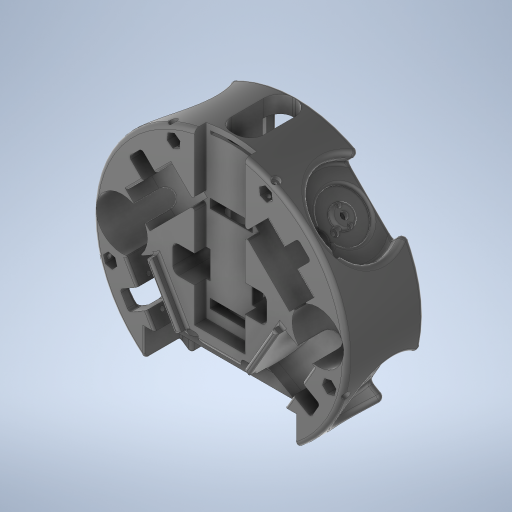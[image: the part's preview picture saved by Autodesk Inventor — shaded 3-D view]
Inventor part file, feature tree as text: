
AUTODESK INVENTOR PART (.ipt)
format: ipt  version: 2023 (Build 270158000, 158)  size: 3,632,128 bytes
history: native  units: mm
features: extrude x76, sketch x74, projected_geometry x35, fillet x19, other x9, chamfer x4, plane x2, mirror x1
ambient origin geometry x8: Origin, YZ Plane, XZ Plane, XY Plane, X Axis, Y Axis, Z Axis, Center Point
bodies: Solid1 (feature_tree)
feature tree (220):
  extrude  "Cilinder"  Depth=54.0mm TaperAngle=0.0deg
  other  "Motor Axis"
  other  "Plano M1"
  other  "Plano M2"
  other  "Plano M3"
  other  "Plano M4"
  extrude  "Roda M1"  Depth=176.0mm
  extrude  "Roda M2"  TaperAngle=60.0deg  [1 undecoded]
  extrude  "Roda M3"  TaperAngle=45.0deg  [1 undecoded]
  extrude  "Roda M4"  TaperAngle=0.0deg  [1 undecoded]
  extrude  "MotorsFitting"  Depth=14.6mm TaperAngle=0.0deg
  fillet  "MotorsCurve"  Radius=55.0mm
  extrude  "Threads M1"  Depth=20.0mm
  extrude  "Threads M2"  Depth=55.0mm
  extrude  "Threads M3"  Depth=20.0mm
  extrude  "Threads M4"  Depth=55.0mm
  extrude  "Threads Head M1"  Depth=20.0mm
  extrude  "Threads Head M2"  Depth=9.4mm
  extrude  "Threads Head M3"  Depth=9.4mm
  extrude  "Threads Head M4"  Depth=23.0mm
  extrude  "Thread Depth M1"  Depth=9.4mm
  extrude  "Thread Depth M2"  Depth=45.0mm
  extrude  "Thread Depth M3"  Depth=45.0mm
  extrude  "Thread Depth M4"  Depth=30.0mm
  extrude  "Threads Nut Head M1"  Depth=32.5mm
  extrude  "Threads Nut Head M2"  Depth=40.0mm TaperAngle=0.0deg
  extrude  "Threads Nut Head M3"  Depth=5.0mm
  extrude  "Threads Nut Head M4"  TaperAngle=0.0deg  [1 undecoded]
  extrude  "Wheel Fitting M1"  Depth=3.0mm
  extrude  "Wheel Fitting M2"  TaperAngle=0.0deg  [1 undecoded]
  extrude  "Wheel Fitting M3"  Depth=30.0mm TaperAngle=360.0deg
  extrude  "Wheel Fitting M4"  Depth=2.0mm
  extrude  "Capacitors"  Depth=6.0mm
  extrude  "Gear Entrance M1"  Depth=19.5mm
  extrude  "Gear Entrance M2"  Depth=10.0mm
  extrude  "Gear Entrance M3"  Depth=2.0mm
  extrude  "Gear Entrance M4"  Depth=2.0mm
  fillet  "Rounding Edges"  Radius=3.0mm
  fillet  "Rounding Motor Entrances"  Radius=6.0mm
  extrude  "Standoff Fitting"  TaperAngle=0.0deg  [1 undecoded]
  extrude  "Standoff Thread M1"  Depth=19.6mm
  extrude  "Standoff Thread M2"  Depth=19.5mm
  extrude  "Standoff Thread M3"  TaperAngle=0.0deg  [1 undecoded]
  extrude  "Standoff Thread M4"  Depth=30.0mm TaperAngle=360.0deg
  other  "Standoff Plane M1"
  other  "Standoff Plane M2"
  other  "Standoff Plane M3"
  other  "Standoff Plane M4"
  extrude  "Standoff Head M1"  Depth=10.0mm
  extrude  "Standoff Head M2"  Depth=2.0mm
  extrude  "Standoff Head M3"  TaperAngle=0.0deg  [1 undecoded]
  extrude  "Standoff Head M4"  Depth=6.0mm
  extrude  "Dribbler Entrance"  Depth=19.5mm
  extrude  "Battery Fitting"  Depth=19.6mm
  fillet  "Motor to Battery Edges"  Radius=3.0mm
  extrude  "Front Kicker"  Depth=11.0mm
  fillet  "Front Edges"  Radius=30.0mm
  extrude  "Cover Inlet"  Depth=10.0mm TaperAngle=0.0deg
  extrude  "Capacitors Holes"  Depth=2.0mm
  extrude  "Dribbler Motor Space"  Depth=2.0mm
  extrude  "IR Holder"  TaperAngle=0.0deg  [1 undecoded]
  fillet  "Dribbler and Kicker Edges"  Radius=19.5mm
  fillet  "Minor Fixes"  Radius=19.5mm
  chamfer  "Dribbler Chanfer"  Distance=30.0mm Angle=360.0deg
  extrude  "Capacitor Cable Fittng 1"  Depth=10.0mm TaperAngle=0.0deg
  fillet  "Capacitor Cable Rounding"  Radius=5.5mm
  extrude  "Special Nut M1"  Depth=5.5mm
  extrude  "Special Nut M2"  Depth=5.5mm
  extrude  "Special Nut M3"  Depth=5.5mm
  extrude  "Special Nut M4"  Depth=5.5mm
  extrude  "Special Nut Cylinder M1"  Depth=5.5mm
  extrude  "Special Nut Cylinder M2"  Depth=5.5mm
  extrude  "Special Nut Cylinder M3"  Depth=5.5mm
  extrude  "Special Nut Cylinder M4"  Depth=4.0mm
  fillet  "Special Nut Rounding"  Radius=4.0mm
  extrude  "Kicker Plate Fit 1"  Depth=4.0mm
  extrude  "Kicker Front Opening"  Depth=17.75mm TaperAngle=0.0deg
  extrude  "Kicker Base Fit"  Depth=4.0mm
  extrude  "Coil and Plinge Fitting"  Depth=4.0mm
  extrude  "Kicker Pkate Plunge Fit"  Depth=17.75mm TaperAngle=0.0deg
  chamfer  "Plunge Entrance 1"  Distance=17.6mm
  chamfer  "Plunge Entrance 2"  Distance=17.6mm
  fillet  "Fillet11"  Radius=15.5mm
  chamfer  "Coil Edges 1"  Distance=17.6mm
  extrude  "Kicker Plate Threads"  Depth=32.0mm
  extrude  "kicker Plate Nut 1"  Depth=2.0mm
  extrude  "Kicker Plate Nut 2"  Depth=2.0mm
  extrude  "Kicker Plunge Fit"  Depth=2.0mm
  fillet  "Kicker Plunge Round"  Radius=68.0mm
  fillet  "Wheel Round"  Radius=50.0mm
  extrude  "Capacitor Cables"  Depth=2.0mm
  fillet  "Capacitor Cable Round 1"  Radius=14.0mm
  fillet  "Capacitor Cable Round 2"  Radius=10.0mm
  extrude  "MotorProtection"  Depth=2.0mm
  fillet  "Motor Protection Round"  Radius=10.0mm
  extrude  "Extrusion86"  Depth=2.0mm TaperAngle=0.0deg
  extrude  "Extrusion87"  Depth=2.0mm
  fillet  "Fillet17"  Radius=10.0mm
  extrude  "Extrusion88"  Depth=2.0mm TaperAngle=0.0deg
  plane  "Work Plane14"
  extrude  "Extrusion89"  Depth=2.0mm
  extrude  "Extrusion91"  Depth=10.0mm
  mirror  "Mirror3"
  fillet  "Fillet18"  Radius=14.0mm
  extrude  "Extrusion92"  Depth=2.0mm
  fillet  "Fillet19"  Radius=2.0mm
  extrude  "Extrusion93"  Depth=2.0mm
  fillet  "Fillet20"  Radius=22.0mm
  extrude  "Extrusion94"  Depth=2.0mm
  extrude  "Extrusion95"  Depth=2.0mm
  sketch  "Sketch1"  dims[d0=176.0mm d1=54.0mm d2=0.0mm]
  sketch  "Sketch3"  dims[d3=180.0mm d4=176.0mm]
  sketch  "Sketch4"  dims[d5=60.0deg d6=60.0deg]
  sketch  "Sketch5"  dims[d8=45.0deg d9=45.0deg]
  sketch  "Sketch6"  dims[d10=55.0mm d11=0.0mm]
  sketch  "Sketch7"  dims[d12=20.0mm d13=14.6mm d14=0.0mm d15=55.0mm]
  sketch  "Sketch8"  dims[d16=0.0mm d17=20.0mm]
  sketch  "Sketch9"  dims[d18=14.6mm d19=0.0mm d20=55.0mm]
  sketch  "Sketch10"  dims[d21=0.0mm d22=20.0mm]
  sketch  "Sketch11"  dims[d23=14.6mm d24=0.0mm d25=55.0mm]
  sketch  "Sketch12"  dims[d26=0.0mm d27=20.0mm]
  sketch  "Sketch13"  dims[d28=14.6mm d29=0.0mm d30=9.4mm]
  sketch  "Sketch14"  dims[d32=9.4mm d33=9.4mm]
  sketch  "Sketch15"  dims[d34=23.0mm d35=23.0mm]
  sketch  "Sketch16"  dims[d37=23.0mm d38=9.4mm]
  sketch  "Sketch17"  dims[d39=23.0mm d40=45.0mm]
  sketch  "Sketch18"  dims[d41=45.0mm d42=45.0mm]
  sketch  "Sketch19"  dims[d43=45.0mm d44=30.0mm]
  sketch  "Sketch20"  dims[d45=30.0mm d46=32.5mm]
  sketch  "Sketch21"  dims[d47=32.5mm d48=40.0mm d49=0.0mm]
  sketch  "Sketch22"  dims[d50=22.5mm d51=5.0mm]
  sketch  "Sketch23"  dims[d52=12.5mm d53=0.0mm]
  sketch  "Sketch24"  dims[d54=19.5mm d55=3.0mm]
  sketch  "Sketch25"  dims[d56=19.6mm d58=0.0mm]
  sketch  "Sketch26"  dims[d59=11.0mm d60=30.0mm d62=360.0deg]
  sketch  "Sketch27"  dims[d64=2.0mm d65=2.0mm]
  sketch  "Sketch28"  dims[d66=6.0mm d67=6.0mm]
  sketch  "Sketch29"  dims[d68=19.5mm d69=19.5mm]
  sketch  "Sketch30"  dims[d70=10.0mm d71=0.0mm d72=2.5mm]
  projected_geometry  "Projected Loop1"
  sketch  "Sketch31"  dims[d73=5.0mm d74=2.0mm]
  projected_geometry  "Projected Loop2"
  sketch  "Sketch32"  dims[d75=2.0mm d76=12.5mm d77=3.0mm d78=6.0mm]
  projected_geometry  "Projected Loop3"
  sketch  "Sketch33"  dims[d79=6.0mm d80=0.0mm]
  projected_geometry  "Projected Loop4"
  sketch  "Sketch34"  dims[d81=19.5mm d82=19.6mm]
  sketch  "Sketch35"  dims[d83=19.5mm d84=19.5mm]
  projected_geometry  "Projected Loop5"
  sketch  "Sketch36"  dims[d85=5.0mm d86=0.0mm]
  projected_geometry  "Projected Loop6"
  sketch  "Sketch37"  dims[d87=11.0mm d88=30.0mm d90=360.0deg]
  projected_geometry  "Projected Loop7"
  sketch  "Sketch38"  dims[d92=10.0mm d93=0.0mm d94=5.0mm]
  projected_geometry  "Projected Loop8"
  sketch  "Sketch39"  dims[d95=12.5mm d96=2.0mm]
  sketch  "Sketch40"  dims[d97=2.0mm d98=0.0mm]
  sketch  "Sketch41"  dims[d99=19.5mm d100=6.0mm]
  sketch  "Sketch42"  dims[d101=6.0mm d102=19.5mm]
  sketch  "Sketch43"  dims[d103=19.5mm d104=19.6mm d105=3.0mm]
  sketch  "Sketch44"  dims[d106=0.0mm d107=11.0mm d108=30.0mm d110=360.0deg]
  projected_geometry  "Projected Loop9"
  projected_geometry  "Projected Loop10"
  sketch  "Sketch45"  dims[d112=5.0mm d113=10.0mm d114=0.0mm]
  sketch  "Sketch46"  dims[d115=5.0mm d116=2.0mm]
  projected_geometry  "Projected Loop11"
  projected_geometry  "Projected Loop12"
  sketch  "Sketch48"  dims[d117=2.0mm d118=6.0mm]
  projected_geometry  "Projected Loop14"
  sketch  "Sketch50"  dims[d119=6.0mm d120=0.0mm d121=19.5mm d122=19.5mm]
  projected_geometry  "Projected Loop15"
  sketch  "Sketch59"  dims[d123=19.5mm]
  sketch  "Sketch64"  dims[d124=12.5mm]
  sketch  "Sketch65"  dims[d125=19.6mm]
  projected_geometry  "Projected Loop27"
  sketch  "Sketch66"  dims[d126=3.0mm]
  projected_geometry  "Projected Loop28"
  sketch  "Sketch67"  dims[d127=0.0mm]
  sketch  "Sketch68"  dims[d128=11.0mm d129=30.0mm d131=360.0deg]
  sketch  "Sketch69"  dims[d133=2.5mm d134=10.0mm d135=0.0mm d136=5.5mm]
  sketch  "Sketch70"  dims[d137=5.5mm d138=5.5mm]
  sketch  "Sketch71"  dims[d139=18.0mm d140=0.0mm d141=5.5mm]
  sketch  "Sketch72"  dims[d142=5.5mm d143=5.5mm]
  projected_geometry  "Projected Loop29"
  sketch  "Sketch73"  dims[d144=18.0mm d145=0.0mm d146=5.5mm]
  sketch  "Sketch74"  dims[d147=5.5mm d148=5.5mm]
  projected_geometry  "Projected Loop30"
  sketch  "Sketch75"  dims[d149=18.0mm d150=0.0mm d151=5.5mm]
  projected_geometry  "Projected Loop31"
  sketch  "Sketch76"  dims[d152=5.5mm d153=5.5mm]
  projected_geometry  "Projected Loop32"
  projected_geometry  "Projected Loop33"
  sketch  "Sketch77"  dims[d154=18.0mm d155=0.0mm d156=4.0mm d157=4.0mm]
  projected_geometry  "Projected Loop34"
  projected_geometry  "Projected Loop35"
  projected_geometry  "Projected Loop36"
  projected_geometry  "Projected Loop37"
  sketch  "Sketch78"  dims[d158=17.75mm d159=0.0mm d160=4.0mm]
  sketch  "Sketch80"  dims[d161=4.0mm d162=17.75mm d163=0.0mm]
  projected_geometry  "Projected Loop38"
  projected_geometry  "Projected Loop39"
  projected_geometry  "Projected Loop40"
  projected_geometry  "Projected Loop41"
  sketch  "Sketch81"  dims[d164=4.0mm d165=4.0mm]
  sketch  "Sketch82"  dims[d166=17.75mm d167=0.0mm d168=4.0mm]
  sketch  "Sketch89"  dims[d169=4.0mm d170=17.75mm d171=0.0mm]
  sketch  "Sketch90"  dims[d172=15.5mm]
  sketch  "Sketch92"  dims[d173=32.0mm d174=17.6mm d175=0.0mm]
  sketch  "Sketch93"  dims[d176=15.5mm]
  sketch  "Sketch95"  dims[d177=32.0mm d178=17.6mm d179=0.0mm d180=15.5mm]
  plane  "Work Plane15"
  projected_geometry  "Projected Loop46"
  projected_geometry  "Projected Loop47"
  projected_geometry  "Projected Loop48"
  sketch  "Sketch97"  dims[d181=32.0mm d182=17.6mm d183=0.0mm]
  sketch  "Sketch98"  dims[d184=15.5mm d185=32.0mm]
  projected_geometry  "Projected Loop49"
  projected_geometry  "Projected Loop50"
  projected_geometry  "Projected Loop51"
  sketch  "Sketch99"  dims[d186=17.6mm d187=0.0mm d188=35.7mm d189=4.15mm d190=68.0mm d191=68.0mm d192=50.0mm d193=0.0mm d195=12.5mm d196=14.0mm d197=0.0mm d198=10.0mm d199=12.5mm d200=10.0mm d201=14.0mm d202=0.0mm d203=12.5mm d204=10.0mm d205=14.0mm d206=0.0mm d207=12.5mm d208=10.0mm d209=14.0mm d210=0.0mm d211=3.0mm d212=2.0mm d213=2.0mm d214=2.0mm d215=22.0mm d216=76.0mm d217=4.22mm d218=72.0mm d219=32.0mm d220=4.22mm d221=8.0mm d222=0.0mm d223=3.0mm d224=3.5mm d225=2.436418mm d226=24.0mm d227=0.0mm d228=3.0mm d229=3.5mm d230=2.436418mm d231=24.0mm d232=0.0mm d233=3.0mm d234=3.5mm d235=2.436418mm d236=24.0mm d237=0.0mm d238=3.0mm d239=3.5mm d240=2.436418mm d241=24.0mm d242=0.0mm d243=90.0mm d244=40.0mm d245=0.0mm d246=55.0mm d247=10.0mm d248=0.0mm d249=2.0mm d250=0.0mm d251=2.0mm d252=0.0mm d253=2.0mm d254=0.0mm d255=2.0mm d256=0.0mm d257=2.0mm d258=1.5mm d259=35.0mm d260=120.0mm d261=0.0mm d262=28.5mm d263=8.0mm d264=0.0mm d265=1.5mm d266=-2.0mm d267=-2.0mm d268=-2.0mm d269=-2.0mm d270=5.5mm d271=4.0mm d272=0.0mm d273=5.5mm d274=4.0mm d275=0.0mm d276=5.5mm d277=4.0mm d278=0.0mm d279=5.5mm d280=4.0mm d281=0.0mm d282=56.5mm d283=12.5mm d284=0.0mm d285=17.0mm d286=10.0mm d287=0.0mm d288=2.0mm d289=3.0mm d299=82.0mm d300=17.453293mm d301=3.490659mm d302=84.0mm d303=17.453293mm d304=3.490659mm d305=8.0mm d306=0.0mm d307=0.4mm d308=22.0mm d309=22.0mm d310=10.0mm d311=0.0mm d317=90.0mm d318=14.0mm d319=0.0mm d320=0.0mm d321=11.0mm d322=0.0mm d327=3.75mm d328=17.11mm d329=0.0mm d330=24.43461mm d331=7.1mm d332=0.0mm d355=2.0mm d356=2.0mm d357=45.0deg d358=3.0mm d359=2.0mm d396=5.5mm d397=10.0mm d398=23.0mm d399=16.0mm d400=56.0mm d401=0.0mm d402=5.5mm d403=0.0mm d404=1.5mm d429=8.1mm d430=16.1mm d431=6.0mm d432=3.0mm d433=0.0mm d434=0.0mm d435=16.1mm d436=8.1mm d437=6.0mm d438=3.0mm d439=0.0mm d440=0.0mm d441=16.1mm d442=8.1mm d443=6.0mm d444=3.0mm d445=0.0mm d446=0.0mm d447=8.1mm d448=16.1mm d449=6.0mm d450=3.0mm d451=0.0mm d452=0.0mm d453=8.1mm d454=5.75mm d455=0.0mm d456=8.1mm d457=5.75mm d458=0.0mm d459=8.1mm d460=5.75mm d461=0.0mm d462=8.1mm d463=5.75mm d464=0.0mm d465=0.9mm d466=29.2mm d467=135.0mm d468=0.0mm d469=14.6mm d470=76.25mm d471=43.2mm d472=7.1mm d473=0.0mm d474=43.2mm d475=7.1mm d476=0.0mm d477=34.5mm d478=79.5mm d479=6.0mm d480=0.0mm d481=30.9mm d482=41.0mm d483=0.0mm d485=29.2mm d486=6.2mm d490=46.1mm d491=0.0mm d492=29.2mm d493=6.2mm d494=3.6mm d495=3.6mm d496=44.8mm d497=0.0mm d498=7.0mm d499=0.0mm d500=6.4mm d501=3.6mm d502=45.0deg d503=6.4mm d504=3.6mm d505=45.0deg d507=10.0mm d508=7.5mm d509=4.6mm d510=60.0deg d511=3.0mm d512=3.0mm d513=18.0mm d514=18.0mm d515=3.0mm d516=3.0mm d517=18.0mm d518=18.0mm d519=3.55mm d520=3.55mm d521=3.55mm d522=3.55mm d523=12.0mm d524=0.0mm d525=5.6mm d526=2.4mm d527=5.6mm d528=2.4mm d529=3.0mm d530=3.0mm d531=1.3mm d532=1.3mm d533=39.8mm d534=0.0mm d535=60.0deg d536=60.0deg d537=120.0deg d538=120.0deg d539=60.0deg d540=60.0deg d541=120.0deg d542=120.0deg d543=10.0mm d544=0.0mm d545=22.0mm d546=20.0mm d547=11.0mm d548=12.5mm d549=10.0mm d550=0.0mm d551=10.0mm d552=3.0mm d553=2.0mm d554=3.0mm d555=18.0mm d556=19.0mm d557=18.0mm d558=19.0mm d559=23.6mm d560=23.6mm d561=7.5mm d562=7.5mm d563=47.0mm d564=0.0mm d565=2.0mm d566=2.0mm d567=4.0mm d568=5.0mm d609=0.0mm d611=5.0mm d612=0.0mm d613=3.75mm d614=0.0mm d616=0.0mm d617=5.0mm d618=3.75mm d619=6.0mm d620=0.0mm d621=1.75mm d622=0.75mm d623=5.5mm d624=9.5mm d625=9.25mm d626=25.9mm d627=8.5mm d628=0.0mm d632=3.0mm d633=0.0mm d636=7.4mm d637=0.0mm d638=3.0mm d639=3.0mm d640=4.0mm d641=3.75mm d642=131.25mm d643=0.0mm d644=-8.0mm d645=5.5mm d646=10.0mm d647=0.0mm d650=10.0mm d651=10.0mm d653=16.0mm d654=2.5mm d655=0.0mm d656=1.0mm d657=2.0mm d664=1.0mm d665=0.0mm d666=19.9mm d667=0.5mm d668=53.9mm d669=25.0mm d670=10.25mm d671=26.12407mm d672=8.0mm d673=90.0deg d674=90.0deg d675=90.0deg d676=90.0deg d677=90.0deg d678=90.0deg d679=90.0deg d680=4.0mm d681=2.0mm d682=29.2mm d683=10.0mm d684=0.0mm d685=2.0mm d686=0.5mm d687=3.0mm d688=3.0mm d689=6.5mm d691=6.5mm d692=4.0mm d693=10.0mm d694=0.0mm d695=5.5mm d696=5.5mm d697=2.0mm d698=2.1mm d699=0.0mm d700=0.0mm d701=4.0mm d702=0.0mm]
note: 9 required parameter values undecoded (feature->parameter linkage not recoverable at this tier; creation-order binding heuristic only, values carry confidence <= 0.55)
